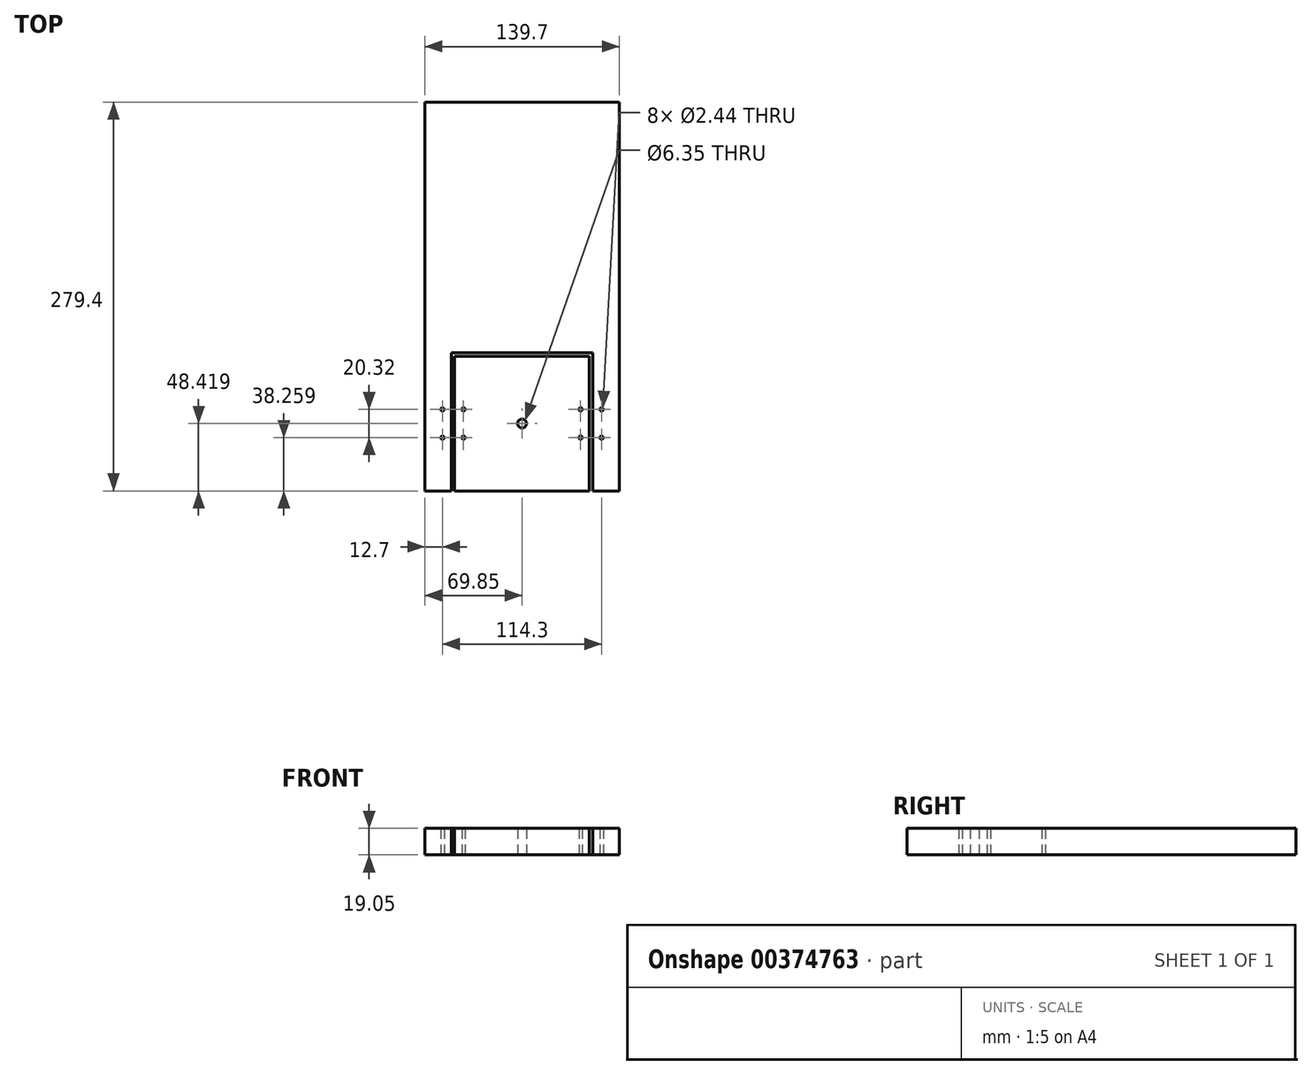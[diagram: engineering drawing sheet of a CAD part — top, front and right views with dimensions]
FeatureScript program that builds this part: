
annotation { "Feature Type Name" : "Feature", "Feature Type Description" : "" }
export const myFeature = defineFeature(function(context is Context, id is Id, definition is map)
    precondition{}
    {
        {
            var Q0;
            Q0=qCreatedBy(makeId("Top.planeOp"),FACE);
            var sketch = newSketch(context, id + "F0", { "sketchPlane" : qUnion([Q0])});
            skLineSegment(sketch, "E0.bottom", {"start": v(69.85, -139.7) * mm, "end": v(50.8, -139.7) * mm});
            skLineSegment(sketch, "E0.top", {"start": v(69.85, 139.7) * mm, "end": v(-69.85, 139.7) * mm});
            skLineSegment(sketch, "E0.left", {"start": v(69.85, -139.7) * mm, "end": v(69.85, 139.7) * mm});
            skLineSegment(sketch, "E0.right", {"start": v(-69.85, -139.7) * mm, "end": v(-69.85, 139.7) * mm});
            skPoint(sketch, "E0.middle", {"position": v(0, 0) * mm});
            skLineSegment(sketch, "E1", {"start": v(-50.8, -139.7) * mm, "end": v(-69.85, -139.7) * mm});
            skLineSegment(sketch, "E2", {"start": v(50.8, -40.48) * mm, "end": v(-50.8, -40.48) * mm});
            skLineSegment(sketch, "E3", {"start": v(-50.8, -40.48) * mm, "end": v(-50.8, -139.7) * mm});
            skLineSegment(sketch, "E4", {"start": v(50.8, -40.48) * mm, "end": v(50.8, -139.7) * mm});
            skLineSegment(sketch, "E5.bottom", {"start": v(-48.42, -139.7) * mm, "end": v(48.42, -139.7) * mm});
            skLineSegment(sketch, "E5.top", {"start": v(-48.42, -42.86) * mm, "end": v(48.42, -42.86) * mm});
            skLineSegment(sketch, "E5.left", {"start": v(-48.42, -139.7) * mm, "end": v(-48.42, -42.86) * mm});
            skLineSegment(sketch, "E5.right", {"start": v(48.42, -139.7) * mm, "end": v(48.42, -42.86) * mm});
            skLineSegment(sketch, "E6.bottom", {"start": v(104.1, -72.23) * mm, "end": v(91.4, -72.23) * mm});
            skLineSegment(sketch, "E6.top", {"start": v(104.1, -110.33) * mm, "end": v(91.4, -110.33) * mm});
            skLineSegment(sketch, "E6.left", {"start": v(104.1, -72.23) * mm, "end": v(104.1, -110.33) * mm});
            skLineSegment(sketch, "E6.right", {"start": v(91.4, -72.23) * mm, "end": v(91.4, -110.33) * mm});
            skLineSegment(sketch, "E7", {"start": v(-48.42, -139.7) * mm, "end": v(48.42, -42.86) * mm});
            skPoint(sketch, "E8", {"position": v(0, -91.28) * mm});
            skLineSegment(sketch, "E9", {"start": v(91.4, -110.33) * mm, "end": v(104.1, -72.23) * mm});
            skPoint(sketch, "E10", {"position": v(97.76, -91.28) * mm});
            skPoint(sketch, "E11", {"position": v(97.76, -81.12) * mm});
            skPoint(sketch, "E12", {"position": v(97.76, -101.44) * mm});
            skPoint(sketch, "E13", {"position": v(57.15, -81.12) * mm});
            skPoint(sketch, "E14", {"position": v(42.07, -81.12) * mm});
            skPoint(sketch, "E15", {"position": v(57.15, -101.44) * mm});
            skPoint(sketch, "E16", {"position": v(42.07, -101.44) * mm});
            skPoint(sketch, "E17", {"position": v(-42.07, -81.12) * mm});
            skPoint(sketch, "E18", {"position": v(-57.15, -81.12) * mm});
            skPoint(sketch, "E19", {"position": v(-57.15, -101.44) * mm});
            skPoint(sketch, "E20", {"position": v(-42.07, -101.44) * mm});
            skSolve(sketch);
        }
        {
            var Q0;
            Q0=makeQuery(id+"F0.imprint","IMPRINT",FACE,{"disambiguationData":[TD([[makeQuery(id+"F0.imprint","IMPRINT",EDGE,{"derivedFrom":sQuery(id+"F0.wireOp",EDGE,"E0.bottom")}),-1.0]])]});
            var Q1;
            Q1=makeQuery(id+"F0.imprint","IMPRINT",FACE,{"disambiguationData":[TD([[makeQuery(id+"F0.imprint","IMPRINT",EDGE,{"derivedFrom":sQuery(id+"F0.wireOp",EDGE,"E5.bottom")}),1.0]])]});
            var Q2;
            Q2=makeQuery(id+"F0.imprint","IMPRINT",FACE,{"disambiguationData":[TD([[makeQuery(id+"F0.imprint","IMPRINT",EDGE,{"derivedFrom":sQuery(id+"F0.wireOp",EDGE,"E5.top")}),-1.0]])]});
            extrude(context, id + "F1", {"entities" : qUnion([Q0, Q1, Q2]), "depth" : 19.05 * mm});
        }
        {
            var Q0;
            Q0=sQuery(id+"F0.wireOp",VERTEX,"E18");
            var Q1;
            Q1=sQuery(id+"F0.wireOp",VERTEX,"E19");
            var Q2;
            Q2=sQuery(id+"F0.wireOp",VERTEX,"E20");
            var Q3;
            Q3=sQuery(id+"F0.wireOp",VERTEX,"E17");
            var Q4;
            Q4=sQuery(id+"F0.wireOp",VERTEX,"E14");
            var Q5;
            Q5=sQuery(id+"F0.wireOp",VERTEX,"E13");
            var Q6;
            Q6=sQuery(id+"F0.wireOp",VERTEX,"E15");
            var Q7;
            Q7=sQuery(id+"F0.wireOp",VERTEX,"E16");
            var Q8;
            Q8=makeQuery(id+"F1.opExtrude","SWEPT_BODY",BODY,{"disambiguationData":[OSD([sQuery(id+"F0.wireOp",EDGE,"E0.bottom"),sQuery(id+"F0.wireOp",EDGE,"E0.top"),sQuery(id+"F0.wireOp",EDGE,"E0.left"),sQuery(id+"F0.wireOp",EDGE,"E0.right"),sQuery(id+"F0.wireOp",EDGE,"E1"),sQuery(id+"F0.wireOp",EDGE,"E2"),sQuery(id+"F0.wireOp",EDGE,"E3"),sQuery(id+"F0.wireOp",EDGE,"E4")])]});
            var Q9;
            Q9=makeQuery(id+"F1.opExtrude","SWEPT_BODY",BODY,{"disambiguationData":[OSD([sQuery(id+"F0.wireOp",EDGE,"E5.bottom"),sQuery(id+"F0.wireOp",EDGE,"E5.top"),sQuery(id+"F0.wireOp",EDGE,"E5.left"),sQuery(id+"F0.wireOp",EDGE,"E5.right")])]});
            hole(context, id + "F2", {"style" : HoleStyle.SIMPLE, "endStyle" : HoleEndStyle.THROUGH, "oppositeDirection" : true, "standardTappedOrClearance" : lookupTablePath({ "standard" : "ANSI", "fit" : "Normal (ASME)", "size" : "#2", "type" : "Clearance" }), "standardBlindInLast" : lookupTablePath({ "fit" : "Free", "standard" : "ANSI", "size" : "#2", "type" : "Clearance" }), "holeDiameter" : 2.44 * mm, "isTappedThrough" : true, "tappedDepth" : 12.7 * mm, "tapClearance" : 3, "locations" : qUnion([Q0, Q1, Q2, Q3, Q4, Q5, Q6, Q7]), "scope" : qUnion([Q8, Q9])});
        }
        {
            var Q0;
            Q0=sQuery(id+"F0.wireOp",VERTEX,"E8");
            var Q1;
            Q1=makeQuery(id+"F1.opExtrude","SWEPT_BODY",BODY,{"disambiguationData":[OSD([sQuery(id+"F0.wireOp",EDGE,"E5.bottom"),sQuery(id+"F0.wireOp",EDGE,"E5.top"),sQuery(id+"F0.wireOp",EDGE,"E5.left"),sQuery(id+"F0.wireOp",EDGE,"E5.right")])]});
            hole(context, id + "F3", {"style" : HoleStyle.SIMPLE, "endStyle" : HoleEndStyle.THROUGH, "oppositeDirection" : true, "holeDiameter" : 6.35 * mm, "isTappedThrough" : true, "tappedDepth" : 12.7 * mm, "tapClearance" : 3, "locations" : qUnion([Q0]), "scope" : qUnion([Q1])});
        }
    });
